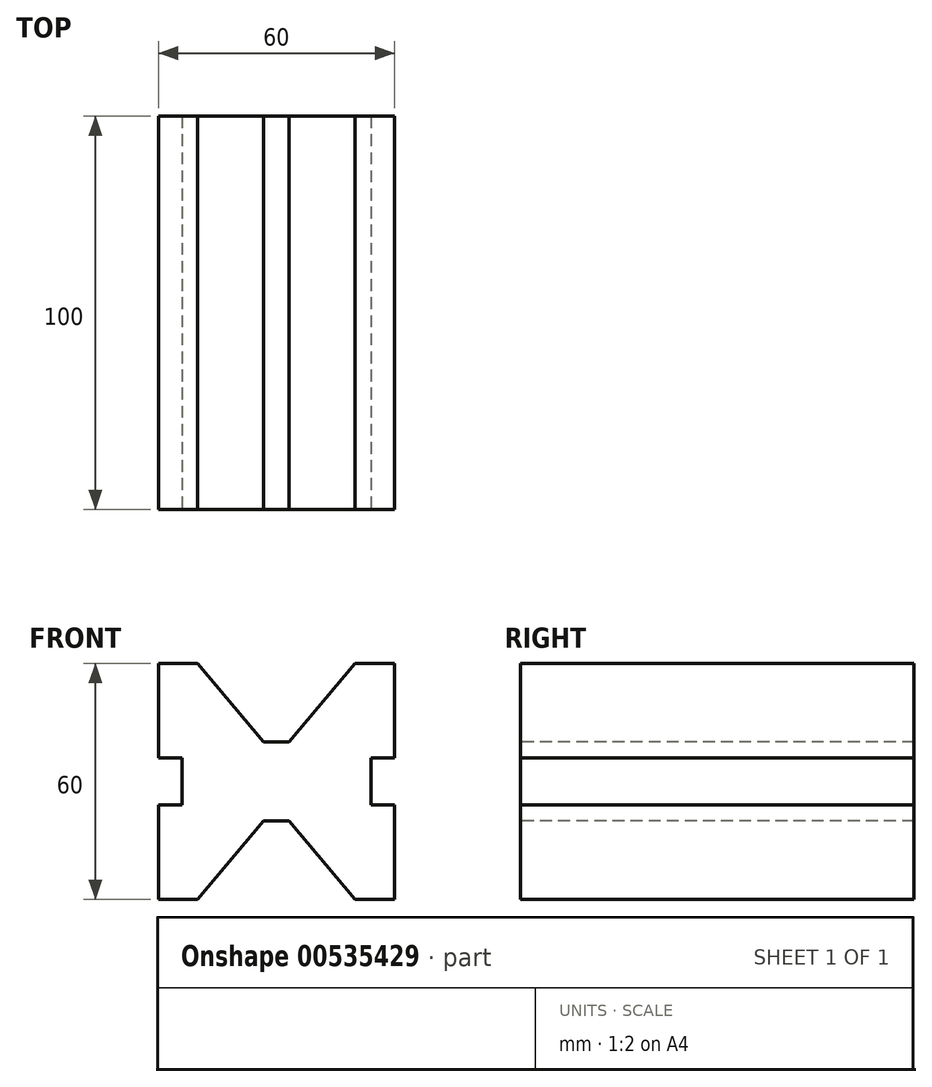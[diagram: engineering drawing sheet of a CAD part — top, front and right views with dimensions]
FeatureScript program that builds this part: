
annotation { "Feature Type Name" : "Feature", "Feature Type Description" : "" }
export const myFeature = defineFeature(function(context is Context, id is Id, definition is map)
    precondition{}
    {
        {
            var Q0;
            Q0=qCreatedBy(makeId("Front.planeOp"),FACE);
            var sketch = newSketch(context, id + "F0", { "sketchPlane" : qUnion([Q0])});
            skLineSegment(sketch, "E0.bottom", {"start": v(-30, 30) * mm, "end": v(-20.03, 30) * mm});
            skLineSegment(sketch, "E0.top", {"start": v(-30, -30) * mm, "end": v(-20, -30) * mm});
            skLineSegment(sketch, "E0.left", {"start": v(-30, 30) * mm, "end": v(-30, 6) * mm});
            skLineSegment(sketch, "E0.right", {"start": v(30, 30) * mm, "end": v(30, 6) * mm});
            skLineSegment(sketch, "E1", {"start": v(0, 30) * mm, "end": v(0, -30) * mm, "construction": true});
            skLineSegment(sketch, "E2", {"start": v(-24, 0) * mm, "end": v(24, 0) * mm, "construction": true});
            skLineSegment(sketch, "E3.0", {"start": v(0, -10) * mm, "end": v(3.24, -10) * mm});
            skLineSegment(sketch, "E4.trimOffspring", {"start": v(3.24, -10) * mm, "end": v(20.03, -30) * mm});
            skLineSegment(sketch, "E5", {"start": v(20.03, -30) * mm, "end": v(30, -30) * mm});
            skLineSegment(sketch, "E6", {"start": v(-30, 6) * mm, "end": v(-24, 6) * mm});
            skLineSegment(sketch, "E7", {"start": v(-24, 6) * mm, "end": v(-24, -6) * mm});
            skLineSegment(sketch, "E8", {"start": v(-24, -6) * mm, "end": v(-30, -6) * mm});
            skLineSegment(sketch, "E9.trimOffspring", {"start": v(-30, -6) * mm, "end": v(-30, -30) * mm});
            skPoint(sketch, "E10.orphan", {"position": v(-30, 0) * mm});
            skLineSegment(sketch, "E11.MirrorCS", {"start": v(30, 6) * mm, "end": v(24, 6) * mm});
            skLineSegment(sketch, "E12.MirrorCS", {"start": v(24, 6) * mm, "end": v(24, -6) * mm});
            skLineSegment(sketch, "E13.MirrorCS", {"start": v(24, -6) * mm, "end": v(30, -6) * mm});
            skLineSegment(sketch, "E14.MirrorCS", {"start": v(0, -10) * mm, "end": v(-3.24, -10) * mm});
            skLineSegment(sketch, "E15.MirrorCS", {"start": v(-3.24, -10) * mm, "end": v(-20.03, -30) * mm});
            skLineSegment(sketch, "E16.MirrorCS", {"start": v(-3.24, 10) * mm, "end": v(-20.03, 30) * mm});
            skLineSegment(sketch, "E17.MirrorCS", {"start": v(3.24, 10) * mm, "end": v(20.03, 30) * mm});
            skLineSegment(sketch, "E18.MirrorCS", {"start": v(0, 10) * mm, "end": v(3.24, 10) * mm});
            skLineSegment(sketch, "E19.MirrorCS", {"start": v(0, 10) * mm, "end": v(-3.24, 10) * mm});
            skLineSegment(sketch, "E20.trimOffspring", {"start": v(20.03, 30) * mm, "end": v(30, 30) * mm});
            skLineSegment(sketch, "E21.trimOffspring", {"start": v(30, -6) * mm, "end": v(30, -30) * mm});
            skPoint(sketch, "E22.orphan", {"position": v(30, 0) * mm});
            skSolve(sketch);
        }
        {
            var Q0;
            Q0 = qSketchRegion(id + "F0", true);
            extrude(context, id + "F1", {"entities" : qUnion([Q0]), "oppositeDirection" : true, "depth" : 100 * mm, "offsetDistance" : 25 * mm});
        }
    });
